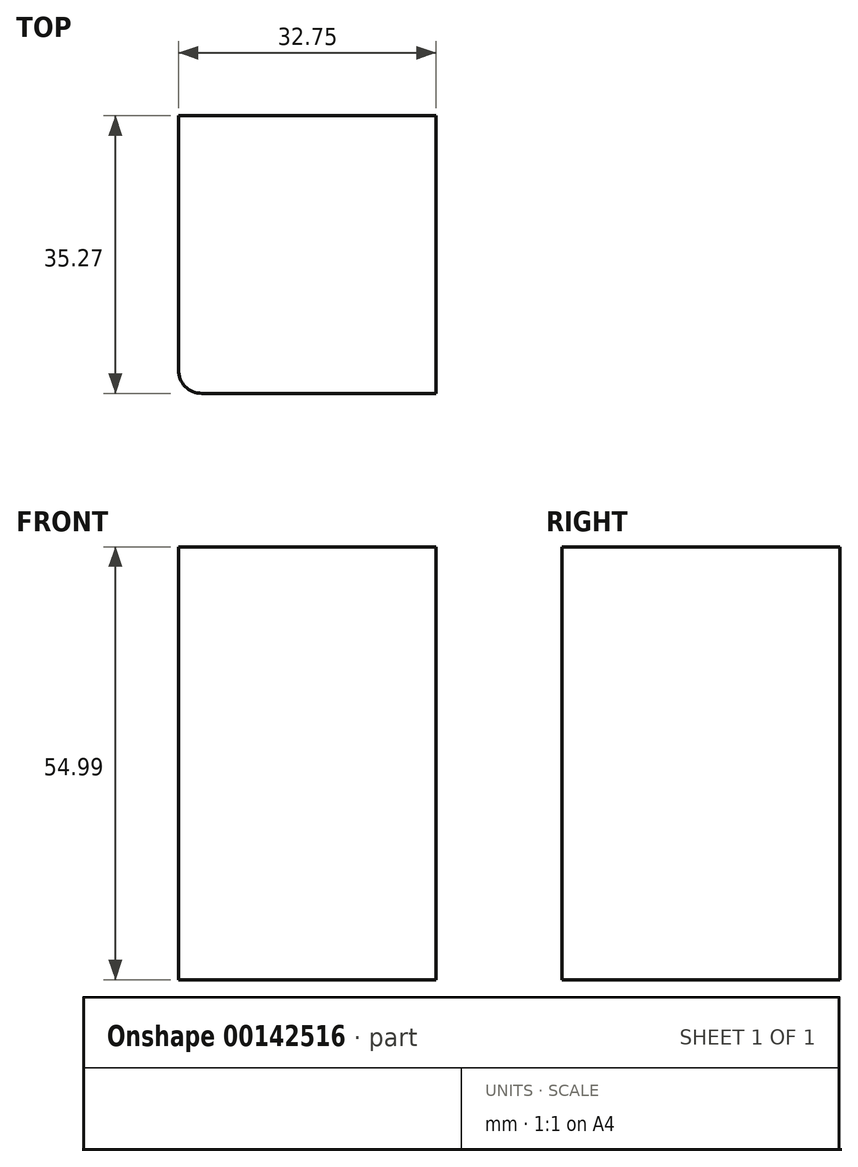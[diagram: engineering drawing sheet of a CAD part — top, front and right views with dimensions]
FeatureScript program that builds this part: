
annotation { "Feature Type Name" : "Feature", "Feature Type Description" : "" }
export const myFeature = defineFeature(function(context is Context, id is Id, definition is map)
    precondition{}
    {
        {
            var Q0;
            Q0=qCreatedBy(makeId("Front.planeOp"),FACE);
            var sketch = newSketch(context, id + "F0", { "sketchPlane" : qUnion([Q0])});
            skLineSegment(sketch, "E0.bottom", {"start": v(0, 18.23) * mm, "end": v(32.75, 18.23) * mm});
            skLineSegment(sketch, "E0.top", {"start": v(0, 73.22) * mm, "end": v(32.75, 73.22) * mm});
            skLineSegment(sketch, "E0.left", {"start": v(0, 18.23) * mm, "end": v(0, 73.22) * mm});
            skLineSegment(sketch, "E0.right", {"start": v(32.75, 18.23) * mm, "end": v(32.75, 73.22) * mm});
            skSolve(sketch);
        }
        {
            var Q0;
            Q0=makeQuery(id+"F0.imprint","IMPRINT",FACE,{"disambiguationData":[TD([[makeQuery(id+"F0.imprint","IMPRINT",EDGE,{"derivedFrom":sQuery(id+"F0.wireOp",EDGE,"E0.bottom")}),1.0]])]});
            extrude(context, id + "F1", {"entities" : qUnion([Q0]), "depth" : 35.27 * mm});
        }
        {
            var Q0;
            Q0=makeQuery(id+"F1.opExtrude","CAP_EDGE",EDGE,{"disambiguationData":[OSD([sQuery(id+"F0.wireOp",EDGE,"E0.left")])],"isStart":false});
            fillet(context, id + "F2", {"entities" : qUnion([Q0]), "radius" : 3 * mm, "tangentPropagation" : true, "allowEdgeOverflow" : false});
        }
    });
